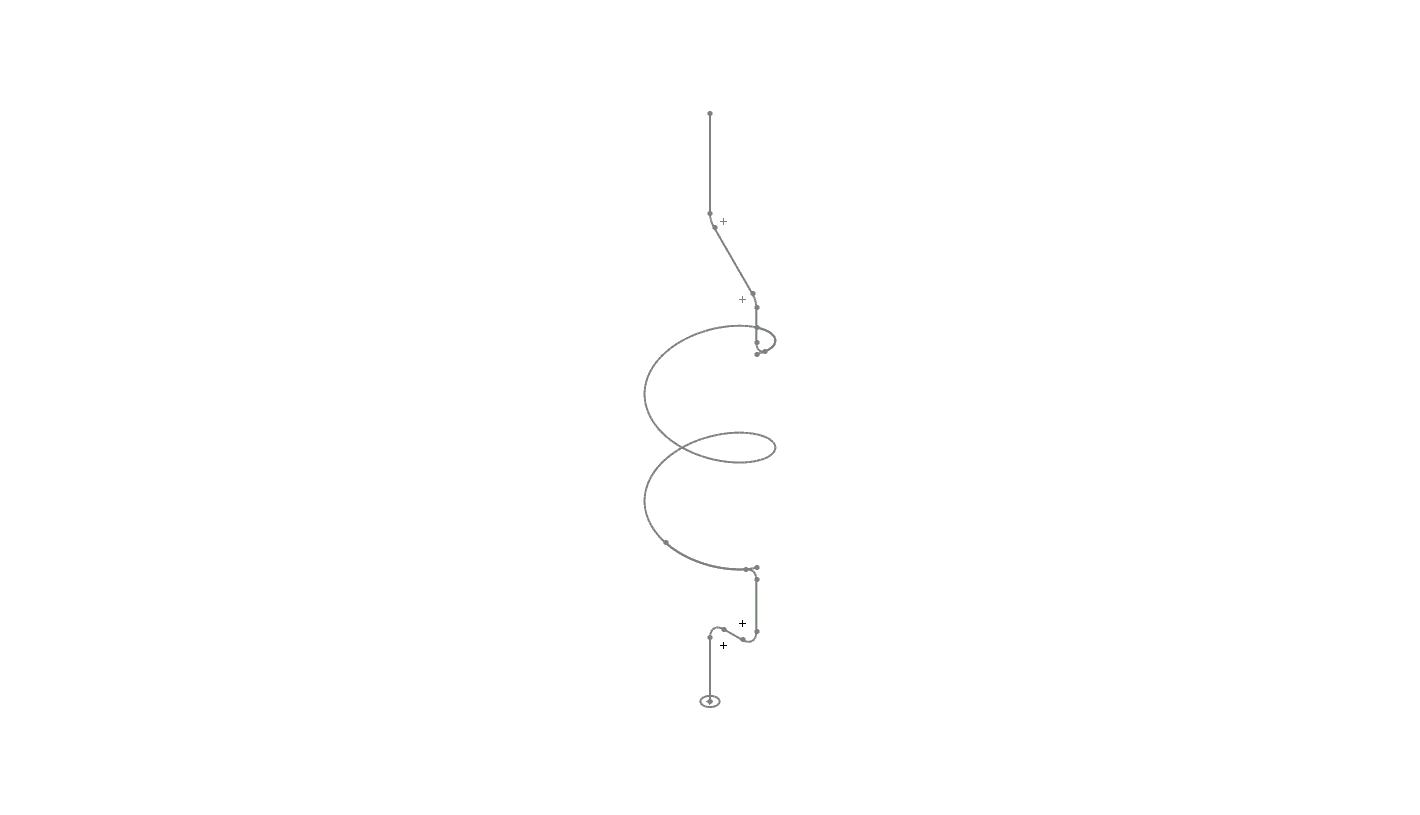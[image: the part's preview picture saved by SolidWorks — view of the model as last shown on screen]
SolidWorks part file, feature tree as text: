
SOLIDWORKS PART (.sldprt)
format: sldprt  version: not decoded by parser v0  size: 238,592 bytes
history: native  units: mm
features: sketch x10, plane x3, material x1, helix x1 + 3 further entries (+9 scaffold rows collapsed)
feature tree (27):
  scaffold x9  (default folders/planes/origin — collapsed)
  material  "Material <nicht festgelegt>"
  plane  "XY-Ebene"
  plane  "XZ-Ebene"
  plane  "YZ-Ebene"
  "Protocol"
  "ProtocolID"
  "Protocol"
  sketch  "Skizze1"  dims[D1=20.0mm]
  helix  "Spirale/Helix1"  Pitch=40mm
  sketch  "3D-Skizze1"  dims[c1.D6=3.0mm c1.D1=~11.723362mm c2.D1=~4.210983mm c3.D1=~14.271162mm c4.D1=~21.970486mm c5.D1=~10.539982mm c6.D1=~13.456037mm c7.D1=~10.603733mm c8.D1=~14.432491mm c9.D1=~20.345844mm c10.D1=~12.76986mm c11.D1=135.0deg c11.D2=50.0mm c11.D3=80.0mm c11.D4=15.0mm c11.D5=15.0mm]
  sketch  "Skizze3"  dims[D1=3.0mm D2=~16.75064mm]
  sketch  "Skizze4"  dims[D1=~5.049775mm]
  sketch  "Skizze5"  dims[D1=~7.627356mm]
  sketch  "Skizze6"  dims[D1=~5.775905mm]
  sketch  "3D-Skizze3"  dims[c1.D1=~16.10925mm c2.D1=3.0mm]
  sketch  "3D-Skizze4"
  sketch  "3D-Skizze6"
  sketch  "3D-Skizze7"  dims[c1.D1=~4.036062mm c2.D1=~26.06361mm c3.D1=~3.699351mm c4.D1=~15.385938mm]
decode coverage: 9 of 11 modeling features carry decoded parameters; 3 rows unclassified (native names shown)
note: ~ marks probable driven/reference dimensions
note: suppression state not decoded; provenance and decode notes live in map.json
